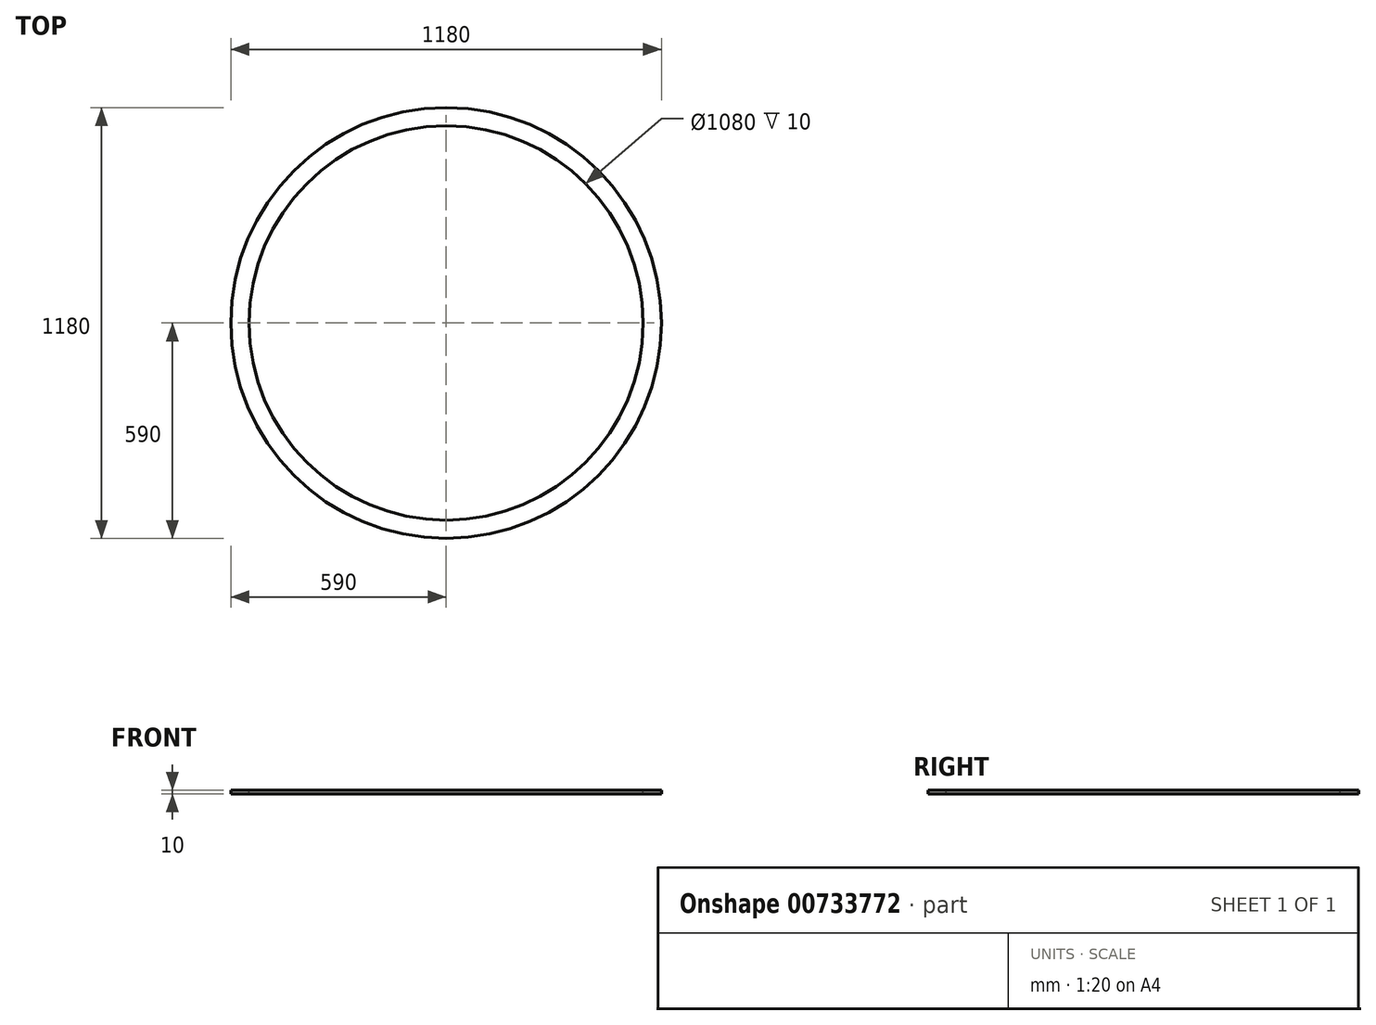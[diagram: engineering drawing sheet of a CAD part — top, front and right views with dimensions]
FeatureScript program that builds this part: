
annotation { "Feature Type Name" : "Feature", "Feature Type Description" : "" }
export const myFeature = defineFeature(function(context is Context, id is Id, definition is map)
    precondition{}
    {
        {
            var Q0;
            Q0=qCreatedBy(makeId("Top.planeOp"),FACE);
            var sketch = newSketch(context, id + "F0", { "sketchPlane" : qUnion([Q0])});
            skCircle(sketch, "E0", {"center": v(0, 0) * mm, "radius": 590 * mm});
            skCircle(sketch, "E1.0", {"center": v(0, 0) * mm, "radius": 540 * mm});
            skSolve(sketch);
        }
        {
            var Q0;
            Q0=makeQuery(id+"F0.imprint","IMPRINT",FACE,{"disambiguationData":[TD([[makeQuery(id+"F0.imprint","IMPRINT",EDGE,{"derivedFrom":sQuery(id+"F0.wireOp",EDGE,"E0")}),1.0]])]});
            extrude(context, id + "F1", {"entities" : qUnion([Q0]), "oppositeDirection" : true, "depth" : 10 * mm, "offsetDistance" : 25 * mm});
        }
    });
